# Revit family: Haworth_Immerse_LedgeTable_Rectangle
name_source: partatom
category: Furniture Systems
revit_build: Autodesk Revit 2018 (Build: 20170223_1515(x64)
units: mm (PartAtom-declared; Revit-internal decimal feet)

## family parameters
Always vertical = Yes
Cut with Voids When Loaded = No
OmniClass Number = 23.40.70.14.64.21
OmniClass Title = Systems Furniture
Part Type = Normal
Room Calculation Point = No
Round Connector Dimension = Use Diameter
Shared = No
Work Plane-Based = No

## types (1)
- 22d 57w 36h
    Actual Depth = 22"
    Actual Height = 36"
    Actual Width = 57"
    Assembly Code = E2020200
    Description = Haworth Immerse Ledge Table Rectangle - 22d 57w 36h
    Manufacturer = Haworth
    Model = THLD-2257
    Revision Number = 1
    Size = Verify Final Dim. w/ Haworth
    URL = https://www.haworth.com
    URL - Product = http://www.haworth.com
    Void Baseline = 30"
    Warranty = http://www.haworth.com

## geometry (parser evidence)
native form markers: Sweep x2
no freeform markers — native parametric forms only
